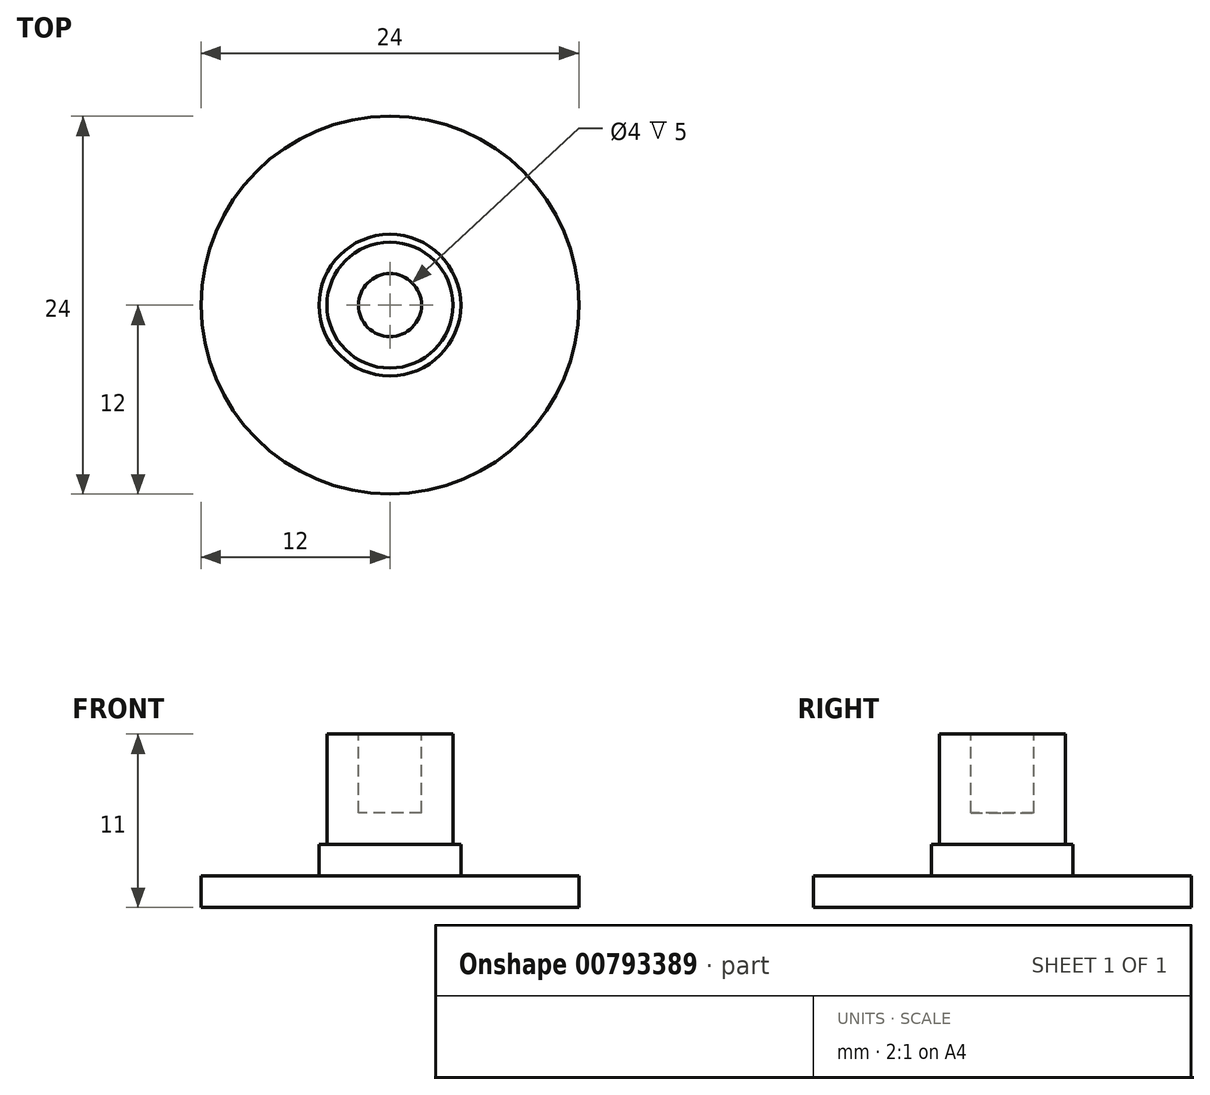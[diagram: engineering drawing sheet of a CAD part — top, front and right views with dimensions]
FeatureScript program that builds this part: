
annotation { "Feature Type Name" : "Feature", "Feature Type Description" : "" }
export const myFeature = defineFeature(function(context is Context, id is Id, definition is map)
    precondition{}
    {
        {
            var Q0;
            Q0=qCreatedBy(makeId("Front.planeOp"),FACE);
            var sketch = newSketch(context, id + "F0", { "sketchPlane" : qUnion([Q0])});
            skLineSegment(sketch, "E0", {"start": v(-12, 0) * mm, "end": v(-12, 2) * mm});
            skLineSegment(sketch, "E1", {"start": v(-4.5, 2) * mm, "end": v(-4.5, 4) * mm});
            skLineSegment(sketch, "E2", {"start": v(-12, 2) * mm, "end": v(-4.5, 2) * mm});
            skLineSegment(sketch, "E3", {"start": v(-12, 0) * mm, "end": v(0, 0) * mm});
            skLineSegment(sketch, "E4", {"start": v(-4, 4) * mm, "end": v(-4, 11) * mm});
            skLineSegment(sketch, "E5", {"start": v(-4.5, 4) * mm, "end": v(-4, 4) * mm});
            skLineSegment(sketch, "E6", {"start": v(-2, 11) * mm, "end": v(-2, 6) * mm});
            skLineSegment(sketch, "E7", {"start": v(-2, 6) * mm, "end": v(0, 6) * mm});
            skLineSegment(sketch, "E8", {"start": v(-4, 11) * mm, "end": v(-2, 11) * mm});
            skLineSegment(sketch, "E9", {"start": v(0, -27.12) * mm, "end": v(0, 30.26) * mm, "construction": true});
            skSolve(sketch);
        }
        {
            var Q0;
            Q0=sQuery(id+"F0.wireOp",EDGE,"E3");
            var Q1;
            Q1=sQuery(id+"F0.wireOp",EDGE,"E0");
            var Q2;
            Q2=sQuery(id+"F0.wireOp",EDGE,"E2");
            var Q3;
            Q3=sQuery(id+"F0.wireOp",EDGE,"E1");
            var Q4;
            Q4=sQuery(id+"F0.wireOp",EDGE,"E5");
            var Q5;
            Q5=sQuery(id+"F0.wireOp",EDGE,"E4");
            var Q6;
            Q6=sQuery(id+"F0.wireOp",EDGE,"E8");
            var Q7;
            Q7=sQuery(id+"F0.wireOp",EDGE,"E6");
            var Q8;
            Q8=sQuery(id+"F0.wireOp",EDGE,"E7");
            var Q9;
            Q9=sQuery(id+"F0.wireOp",EDGE,"E9");
            revolve(context, id + "F1", {"bodyType" : ToolBodyType.SURFACE, "surfaceOperationType" : NewSurfaceOperationType.NEW, "surfaceEntities" : qUnion([Q0, Q1, Q2, Q3, Q4, Q5, Q6, Q7, Q8]), "axis" : qUnion([Q9]), "revolveType" : RevolveType.FULL});
        }
    });
